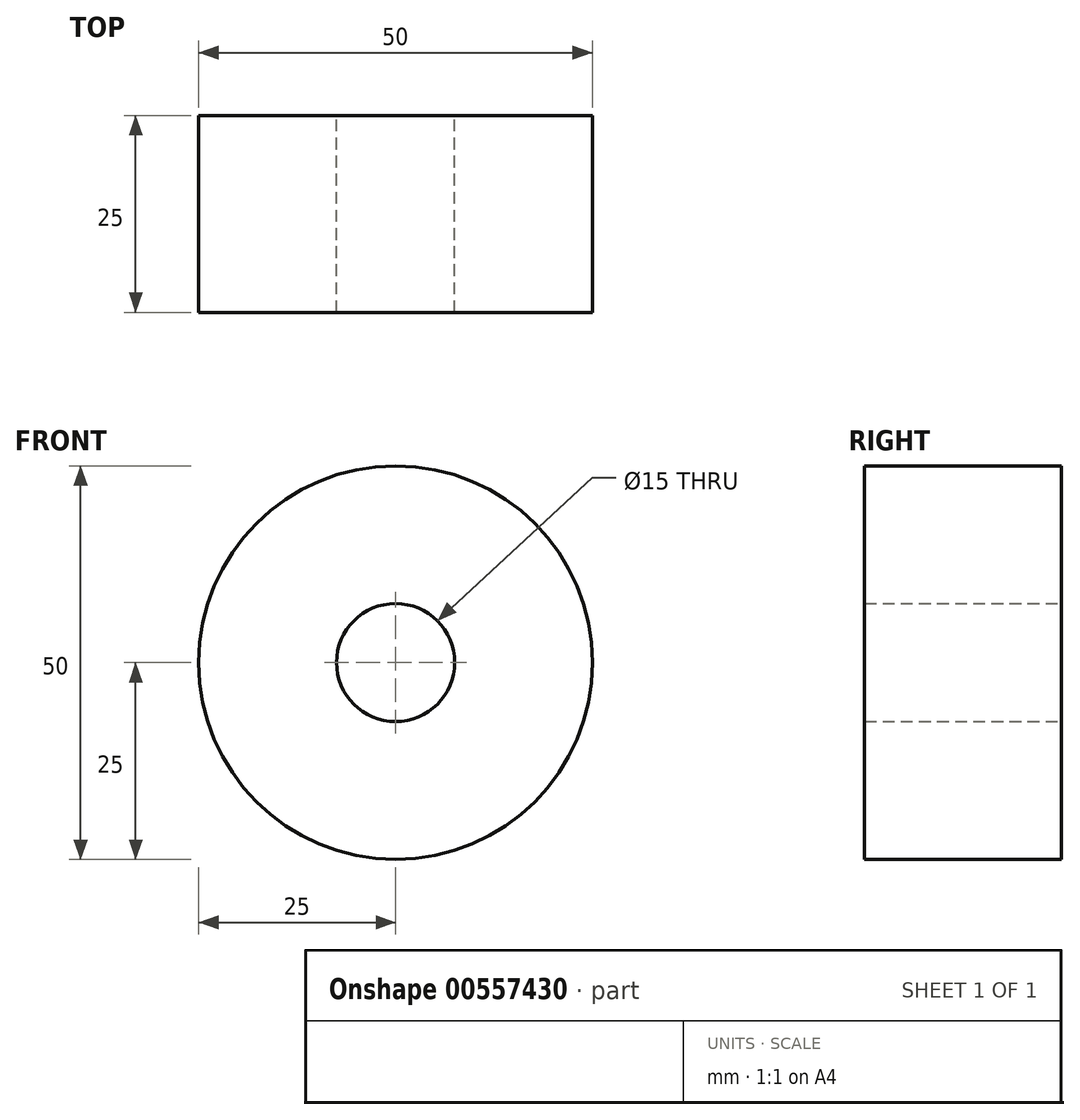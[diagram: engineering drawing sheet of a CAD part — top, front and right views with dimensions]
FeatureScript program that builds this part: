
annotation { "Feature Type Name" : "Feature", "Feature Type Description" : "" }
export const myFeature = defineFeature(function(context is Context, id is Id, definition is map)
    precondition{}
    {
        {
            var Q0;
            Q0=qCreatedBy(makeId("Front.planeOp"),FACE);
            var sketch = newSketch(context, id + "F0", { "sketchPlane" : qUnion([Q0])});
            skCircle(sketch, "E0", {"center": v(0, 0) * mm, "radius": 25 * mm});
            skCircle(sketch, "E1", {"center": v(0, 0) * mm, "radius": 7.5 * mm});
            skSolve(sketch);
        }
        {
            var Q0;
            Q0=makeQuery(id+"F0.imprint","IMPRINT",FACE,{"disambiguationData":[TD([[makeQuery(id+"F0.imprint","IMPRINT",EDGE,{"derivedFrom":sQuery(id+"F0.wireOp",EDGE,"E0")}),1.0]])]});
            extrude(context, id + "F1", {"entities" : qUnion([Q0]), "endBound" : BoundingType.SYMMETRIC, "depth" : 25 * mm, "offsetDistance" : 25 * mm});
        }
    });
